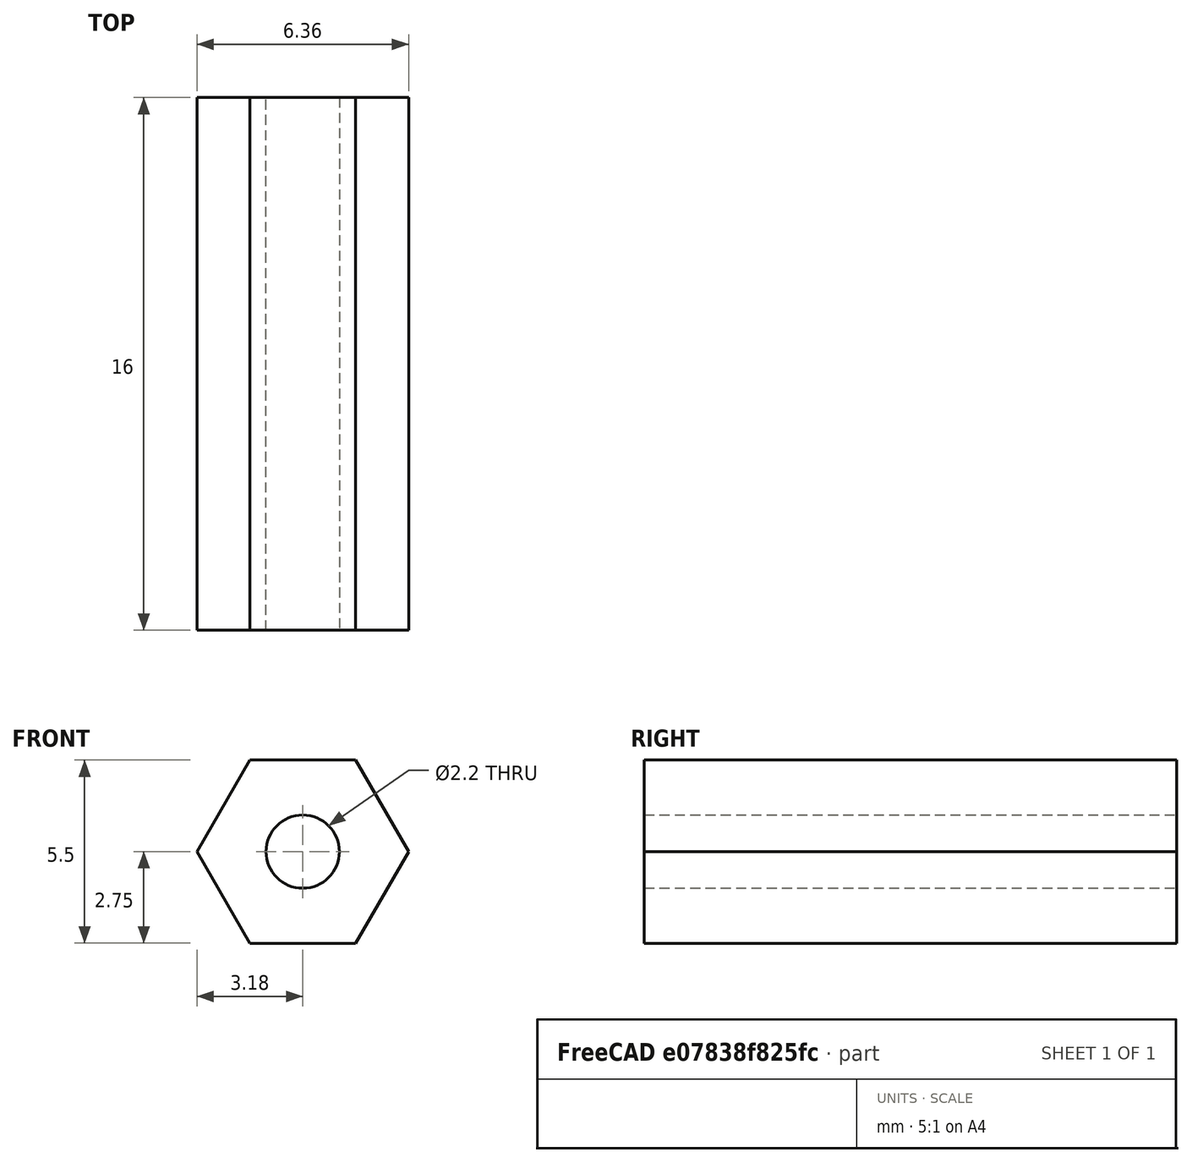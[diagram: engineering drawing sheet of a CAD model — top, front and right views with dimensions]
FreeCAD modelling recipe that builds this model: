
FCSTD DOCUMENT  (FreeCAD 0.21R33771 (Git))
Label: espacador-22-16
License: All rights reserved
LicenseURL: https://en.wikipedia.org/wiki/All_rights_reserved
objects: Sketcher::SketchObject×1, PartDesign::Pad×1, PartDesign::Body×1
note: 4 computed .brp shape members not serialized (recipe doc carries the construction recipe); baked Part::Feature solids carry a one-line shape summary decoded from their .brp

FEATURE [Sketcher::SketchObject] Sketch
  FullyConstrained = true
  MapMode = 5
  Placement = pos=(0,0,0) rot=(1,0,0;1.5708rad)
  Support = -> [XZ_Plane]
  sketch-geometry (12):
    g0: LineSegment StartX=-1.59 StartY=-2.75396 StartZ=0 EndX=1.59 EndY=-2.75396 EndZ=0
    g1: LineSegment StartX=1.59 StartY=-2.75396 StartZ=0 EndX=3.18 EndY=0 EndZ=0
    g2: LineSegment StartX=3.18 StartY=0 StartZ=0 EndX=1.59 EndY=2.75396 EndZ=0
    g3: LineSegment StartX=1.59 StartY=2.75396 StartZ=0 EndX=-1.59 EndY=2.75396 EndZ=0
    g4: LineSegment StartX=-1.59 StartY=2.75396 StartZ=0 EndX=-3.18 EndY=0 EndZ=0
    g5: LineSegment StartX=-3.18 StartY=-1e-16 StartZ=0 EndX=-1.59 EndY=-2.75396 EndZ=0
    g6: Circle CenterX=0 CenterY=0 CenterZ=0 NormalX=0 NormalY=0 NormalZ=1 AngleXU=0 Radius=3.18
    g7: Circle CenterX=0 CenterY=0 CenterZ=0 NormalX=0 NormalY=0 NormalZ=1 AngleXU=0 Radius=1.1
    g8: LineSegment StartX=-1.1 StartY=1.1 StartZ=0 EndX=1.1 EndY=1.1 EndZ=0
    g9: LineSegment StartX=1.1 StartY=1.1 StartZ=0 EndX=1.1 EndY=-1.1 EndZ=0
    g10: LineSegment StartX=1.1 StartY=-1.1 StartZ=0 EndX=-1.1 EndY=-1.1 EndZ=0
    g11: LineSegment StartX=-1.1 StartY=-1.1 StartZ=0 EndX=-1.1 EndY=1.1 EndZ=0
  constraints (30):
    c: Coincident(g0,g1)
    c: Coincident(g1,g2)
    c: Coincident(g2,g3)
    c: Coincident(g3,g4)
    c: Coincident(g4,g5)
    c: Coincident(g5,g0)
    c: Equal(g0, g1-g5) x5
    c: PointOnObject(g0,g6)
    c: PointOnObject(g1,g6)
    c: PointOnObject(g2,g6)
    c: PointOnObject(g3,g6)
    c: PointOnObject(g4,g6)
    c: PointOnObject(g5,g6)
    c: Coincident(g6,g-1)
    c: Horizontal(g0)
    c: Coincident(g7,g6)
    c: Coincident(g8,g9)
    c: Coincident(g9,g10)
    c: Coincident(g10,g11)
    c: Coincident(g11,g8)
    c: Horizontal(g8)
    c: Horizontal(g10)
    c: Vertical(g9)
    c: Vertical(g11)
    c: Tangent(g8,g7)
    c: Tangent(g7,g11)
    c: Tangent(g10,g7)
    c: Tangent(g9,g7)
    c: Diameter(g7) = 2.2
    c: DistanceX(g3,g3) = 3.18
FEATURE [PartDesign::Pad] Pad
  Direction = (0,-1,-2e-16)
  Length = 16
  Length2 = 10
  Placement = pos=(0,0,0) rot=(1,0,0;1.5708rad)
  Profile = -> Sketch
  ReferenceAxis = -> Sketch [N_Axis]
  Type = 0
FEATURE [PartDesign::Body] Body
  Group = -> [Sketch,Pad]
  Origin = -> Origin
  Tip = -> Pad
